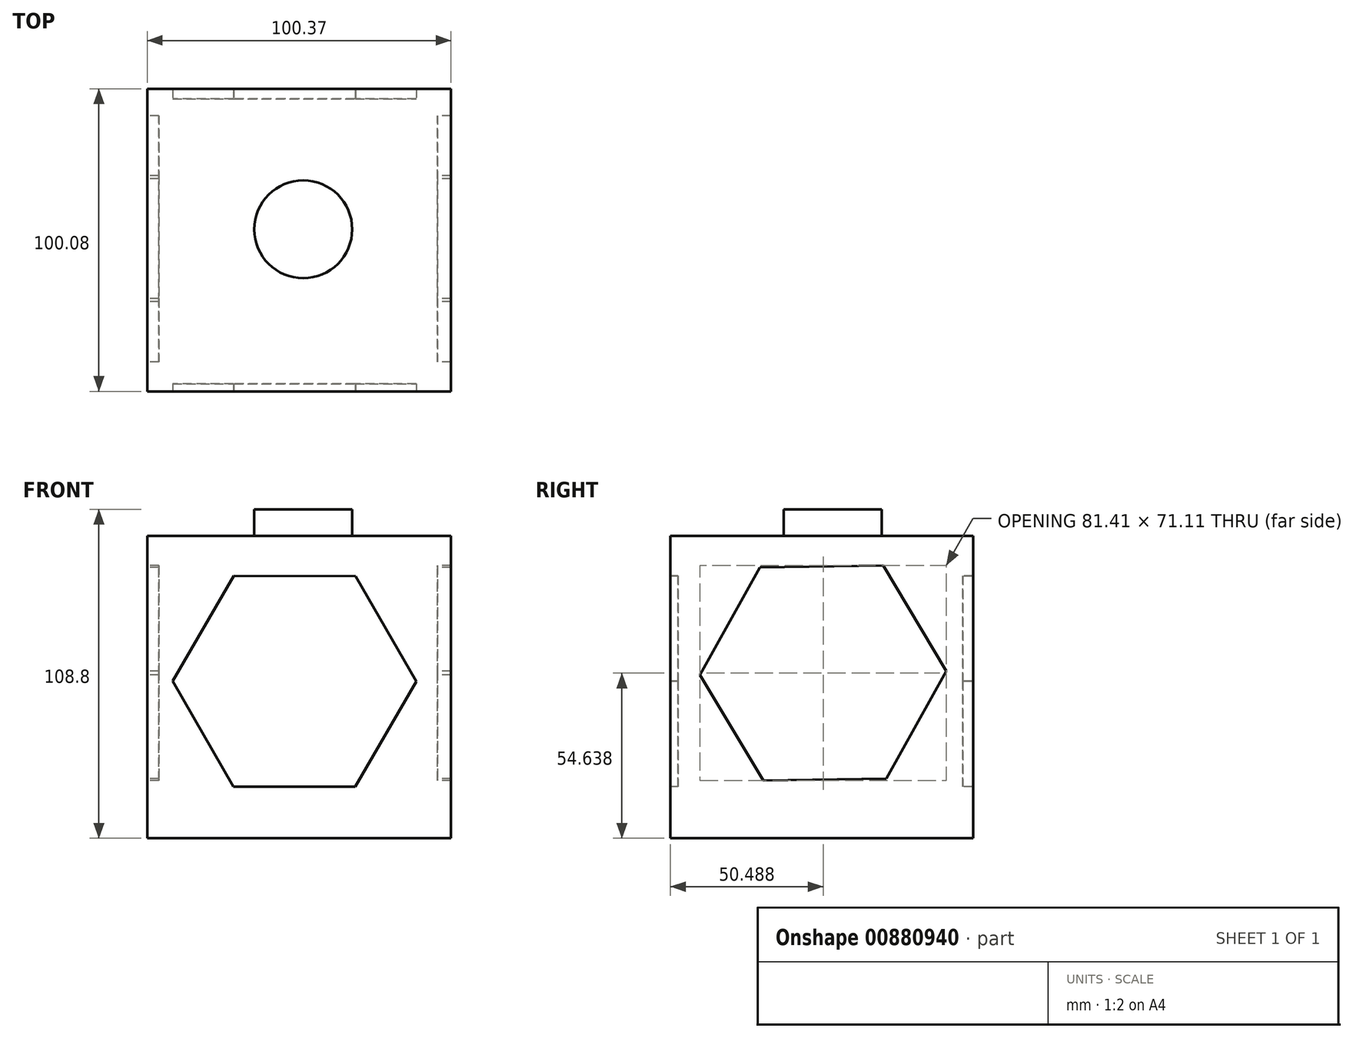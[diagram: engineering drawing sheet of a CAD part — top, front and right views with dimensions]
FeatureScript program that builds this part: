
annotation { "Feature Type Name" : "Feature", "Feature Type Description" : "" }
export const myFeature = defineFeature(function(context is Context, id is Id, definition is map)
    precondition{}
    {
        {
            var Q0;
            Q0=qCreatedBy(makeId("Top.planeOp"),FACE);
            var sketch = newSketch(context, id + "F0", { "sketchPlane" : qUnion([Q0])});
            skLineSegment(sketch, "E0.bottom", {"start": v(-70.02, -63.8) * mm, "end": v(30.35, -63.8) * mm});
            skLineSegment(sketch, "E0.top", {"start": v(-70.02, 36.27) * mm, "end": v(30.35, 36.27) * mm});
            skLineSegment(sketch, "E0.left", {"start": v(-70.02, -63.8) * mm, "end": v(-70.02, 36.27) * mm});
            skLineSegment(sketch, "E0.right", {"start": v(30.35, -63.8) * mm, "end": v(30.35, 36.27) * mm});
            skSolve(sketch);
        }
        {
            var Q0;
            Q0 = qSketchRegion(id + "F0", true);
            extrude(context, id + "F1", {"entities" : qUnion([Q0]), "depth" : 100 * mm, "offsetDistance" : 25 * mm});
        }
        {
            var Q0;
            Q0=makeQuery(id+"F1.opExtrude","SWEPT_FACE",FACE,{"disambiguationData":[OSD([sQuery(id+"F0.wireOp",EDGE,"E0.bottom")])]});
            var sketch = newSketch(context, id + "F2", { "sketchPlane" : qUnion([Q0])});
            skCircle(sketch, "E1.cCircle", {"center": v(-21.41, 51.87) * mm, "radius": 34.84 * mm, "construction": true});
            skLineSegment(sketch, "E1.0", {"start": v(-1.24, 86.68) * mm, "end": v(18.81, 51.8) * mm});
            skLineSegment(sketch, "E1.1", {"start": v(18.81, 51.8) * mm, "end": v(-1.36, 17) * mm});
            skLineSegment(sketch, "E1.2", {"start": v(-1.36, 17) * mm, "end": v(-41.58, 17.07) * mm});
            skLineSegment(sketch, "E1.3", {"start": v(-41.58, 17.07) * mm, "end": v(-61.64, 51.94) * mm});
            skLineSegment(sketch, "E1.4", {"start": v(-61.64, 51.94) * mm, "end": v(-41.47, 86.74) * mm});
            skLineSegment(sketch, "E1.5", {"start": v(-41.47, 86.74) * mm, "end": v(-1.24, 86.68) * mm});
            skPoint(sketch, "E1.0.midPoint", {"position": v(8.78, 69.24) * mm});
            skSolve(sketch);
        }
        {
            var Q0;
            Q0 = qSketchRegion(id + "F2", true);
            extrude(context, id + "F3", {"entities" : qUnion([Q0]), "operationType" : NewBodyOperationType.REMOVE, "oppositeDirection" : true, "depth" : 114 * mm, "offsetDistance" : 25 * mm});
        }
        {
            var Q0;
            Q0=makeQuery(id+"F1.opExtrude","SWEPT_FACE",FACE,{"disambiguationData":[OSD([sQuery(id+"F0.wireOp",EDGE,"E0.left")])]});
            var sketch = newSketch(context, id + "F4", { "sketchPlane" : qUnion([Q0])});
            skLineSegment(sketch, "E2.bottom", {"start": v(-32.86, 97.47) * mm, "end": v(61.28, 97.47) * mm});
            skLineSegment(sketch, "E2.top", {"start": v(-32.86, 2.53) * mm, "end": v(61.28, 2.53) * mm});
            skLineSegment(sketch, "E2.left", {"start": v(-32.86, 97.47) * mm, "end": v(-32.86, 2.53) * mm});
            skLineSegment(sketch, "E2.right", {"start": v(61.28, 97.47) * mm, "end": v(61.28, 2.53) * mm});
            skSolve(sketch);
        }
        {
            var Q0;
            Q0 = qSketchRegion(id + "F4", true);
            extrude(context, id + "F5", {"entities" : qUnion([Q0]), "operationType" : NewBodyOperationType.ADD, "oppositeDirection" : true, "depth" : 95 * mm, "offsetDistance" : 25 * mm});
        }
        {
            var Q0;
            Q0=makeQuery(id+"F1.opExtrude","SWEPT_FACE",FACE,{"disambiguationData":[OSD([sQuery(id+"F0.wireOp",EDGE,"E0.left")])]});
            var sketch = newSketch(context, id + "F6", { "sketchPlane" : qUnion([Q0])});
            skCircle(sketch, "E3.cCircle", {"center": v(13.32, 54.64) * mm, "radius": 35.25 * mm, "construction": true});
            skLineSegment(sketch, "E3.0", {"start": v(34.2, 89.59) * mm, "end": v(54.03, 54.03) * mm});
            skLineSegment(sketch, "E3.1", {"start": v(54.03, 54.03) * mm, "end": v(33.15, 19.09) * mm});
            skLineSegment(sketch, "E3.2", {"start": v(33.15, 19.09) * mm, "end": v(-7.55, 19.7) * mm});
            skLineSegment(sketch, "E3.3", {"start": v(-7.55, 19.7) * mm, "end": v(-27.38, 55.24) * mm});
            skLineSegment(sketch, "E3.4", {"start": v(-27.38, 55.24) * mm, "end": v(-6.5, 90.2) * mm});
            skLineSegment(sketch, "E3.5", {"start": v(-6.5, 90.2) * mm, "end": v(34.2, 89.59) * mm});
            skPoint(sketch, "E3.0.midPoint", {"position": v(44.11, 71.8) * mm});
            skSolve(sketch);
        }
        {
            var Q0;
            Q0 = qSketchRegion(id + "F6", true);
            extrude(context, id + "F7", {"entities" : qUnion([Q0]), "operationType" : NewBodyOperationType.REMOVE, "oppositeDirection" : true, "depth" : 134 * mm, "offsetDistance" : 25 * mm});
        }
        {
            var Q0;
            Q0=makeQuery(id+"F1.opExtrude","CAP_FACE",FACE,{"disambiguationData":[OSD([sQuery(id+"F0.wireOp",EDGE,"E0.bottom"),sQuery(id+"F0.wireOp",EDGE,"E0.top"),sQuery(id+"F0.wireOp",EDGE,"E0.left"),sQuery(id+"F0.wireOp",EDGE,"E0.right")])],"isStart":false});
            var sketch = newSketch(context, id + "F8", { "sketchPlane" : qUnion([Q0])});
            skLineSegment(sketch, "E4.bottom", {"start": v(-66.17, 32.71) * mm, "end": v(25.9, 32.71) * mm});
            skLineSegment(sketch, "E4.top", {"start": v(-66.17, -60.25) * mm, "end": v(25.9, -60.25) * mm});
            skLineSegment(sketch, "E4.left", {"start": v(-66.17, 32.71) * mm, "end": v(-66.17, -60.25) * mm});
            skLineSegment(sketch, "E4.right", {"start": v(25.9, 32.71) * mm, "end": v(25.9, -60.25) * mm});
            skSolve(sketch);
        }
        {
            var Q0;
            Q0 = qSketchRegion(id + "F8", true);
            extrude(context, id + "F9", {"entities" : qUnion([Q0]), "operationType" : NewBodyOperationType.ADD, "oppositeDirection" : true, "depth" : 94.6 * mm, "offsetDistance" : 25 * mm});
        }
        {
            var Q0;
            Q0=makeQuery(id+"F1.opExtrude","CAP_FACE",FACE,{"disambiguationData":[OSD([sQuery(id+"F0.wireOp",EDGE,"E0.bottom"),sQuery(id+"F0.wireOp",EDGE,"E0.top"),sQuery(id+"F0.wireOp",EDGE,"E0.left"),sQuery(id+"F0.wireOp",EDGE,"E0.right")])],"isStart":false});
            var sketch = newSketch(context, id + "F10", { "sketchPlane" : qUnion([Q0])});
            skCircle(sketch, "E5", {"center": v(-18.5, -10.21) * mm, "radius": 16.18 * mm});
            skSolve(sketch);
        }
        {
            var Q0;
            Q0 = qSketchRegion(id + "F10", true);
            extrude(context, id + "F11", {"entities" : qUnion([Q0]), "operationType" : NewBodyOperationType.ADD, "depth" : 8.8 * mm, "offsetDistance" : 25 * mm});
        }
    });
